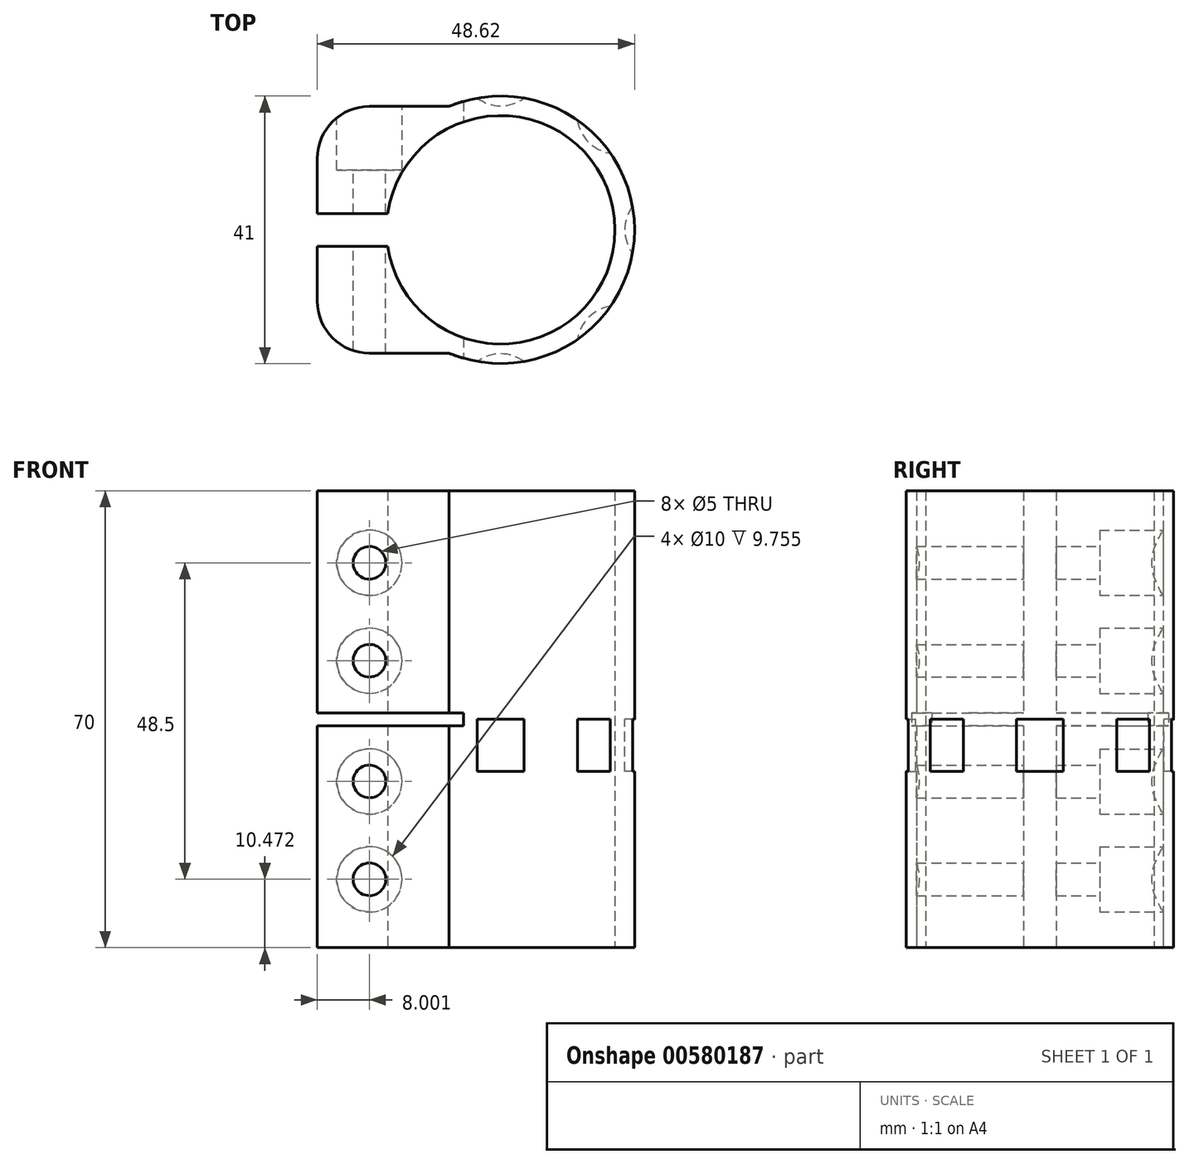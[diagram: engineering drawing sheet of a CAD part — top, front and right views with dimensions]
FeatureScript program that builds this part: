
annotation { "Feature Type Name" : "Feature", "Feature Type Description" : "" }
export const myFeature = defineFeature(function(context is Context, id is Id, definition is map)
    precondition{}
    {
        {
            var Q0;
            Q0=qCreatedBy(makeId("Top.planeOp"),FACE);
            var sketch = newSketch(context, id + "F0", { "sketchPlane" : qUnion([Q0])});
            skArc(sketch, "E0", {"start": v(-17.32, -2.5) * mm, "mid": v(17.5, 0) * mm, "end": v(-17.32, 2.5) * mm});
            skArc(sketch, "E1", {"start": v(-7.92, -18.9) * mm, "mid": v(20.5, 0) * mm, "end": v(-7.92, 18.9) * mm});
            skLineSegment(sketch, "E2", {"start": v(-7.92, 18.9) * mm, "end": v(-20.12, 18.9) * mm});
            skLineSegment(sketch, "E3", {"start": v(-28.12, 10.9) * mm, "end": v(-28.12, 2.5) * mm});
            skLineSegment(sketch, "E4", {"start": v(-28.12, 2.5) * mm, "end": v(-17.32, 2.5) * mm});
            skPoint(sketch, "E5.visualSharp", {"position": v(-28.12, 18.9) * mm});
            skArc(sketch, "E5.filletArc", {"start": v(-20.12, 18.9) * mm, "mid": v(-25.78, 16.57) * mm, "end": v(-28.12, 10.9) * mm});
            skLineSegment(sketch, "E6", {"start": v(0, 0) * mm, "end": v(46.32, 0) * mm, "construction": true});
            skPoint(sketch, "E7.newPointA", {"position": v(-28.12, 10.9) * mm});
            skPoint(sketch, "E7.newPointB", {"position": v(-20.12, 18.9) * mm});
            skLineSegment(sketch, "E8.MirrorCS", {"start": v(-28.12, -2.5) * mm, "end": v(-17.32, -2.5) * mm});
            skLineSegment(sketch, "E9.MirrorCS", {"start": v(-28.12, -10.9) * mm, "end": v(-28.12, -2.5) * mm});
            skArc(sketch, "E10.MirrorCS", {"start": v(-20.12, -18.9) * mm, "mid": v(-25.78, -16.57) * mm, "end": v(-28.12, -10.9) * mm});
            skLineSegment(sketch, "E11.MirrorCS", {"start": v(-7.92, -18.9) * mm, "end": v(-20.12, -18.9) * mm});
            skSolve(sketch);
        }
        {
            var Q0;
            Q0 = qSketchRegion(id + "F0", true);
            extrude(context, id + "F1", {"entities" : qUnion([Q0]), "endBound" : BoundingType.SYMMETRIC, "depth" : 70 * mm, "offsetDistance" : 25 * mm});
        }
        {
            var Q0;
            Q0=makeQuery(id+"F1.opExtrude","SWEPT_FACE",FACE,{"disambiguationData":[OSD([sQuery(id+"F0.wireOp",EDGE,"E2")])]});
            var sketch = newSketch(context, id + "F2", { "sketchPlane" : qUnion([Q0])});
            skPoint(sketch, "E12", {"position": v(20.12, 23.97) * mm});
            skPoint(sketch, "E13", {"position": v(20.12, 8.97) * mm});
            skPoint(sketch, "E14", {"position": v(20.12, -9.53) * mm});
            skPoint(sketch, "E15", {"position": v(20.12, -24.53) * mm});
            skPoint(sketch, "E16", {"position": v(0, -0.28) * mm});
            skSolve(sketch);
        }
        {
            var Q0;
            Q0=sQuery(id+"F2.wireOp",VERTEX,"E12");
            var Q1;
            Q1=sQuery(id+"F2.wireOp",VERTEX,"E13");
            var Q2;
            Q2=sQuery(id+"F2.wireOp",VERTEX,"E14");
            var Q3;
            Q3=sQuery(id+"F2.wireOp",VERTEX,"E15");
            var Q4;
            Q4=makeQuery(id+"F1.opExtrude","SWEPT_BODY",BODY,{"disambiguationData":[OSD([sQuery(id+"F0.wireOp",EDGE,"E0"),sQuery(id+"F0.wireOp",EDGE,"E1"),sQuery(id+"F0.wireOp",EDGE,"E2"),sQuery(id+"F0.wireOp",EDGE,"E3"),sQuery(id+"F0.wireOp",EDGE,"E4"),sQuery(id+"F0.wireOp",EDGE,"E5.filletArc"),sQuery(id+"F0.wireOp",EDGE,"E8.MirrorCS"),sQuery(id+"F0.wireOp",EDGE,"E9.MirrorCS"),sQuery(id+"F0.wireOp",EDGE,"E10.MirrorCS"),sQuery(id+"F0.wireOp",EDGE,"E11.MirrorCS")])]});
            hole(context, id + "F3", {"style" : HoleStyle.C_BORE, "endStyle" : HoleEndStyle.THROUGH, "holeDiameter" : 5 * mm, "cBoreDiameter" : 10 * mm, "cBoreDepth" : 8 * mm, "majorDiameter" : 5 * mm, "isTappedThrough" : true, "tappedDepth" : 12 * mm, "tapClearance" : 3, "locations" : qUnion([Q0, Q1, Q2, Q3]), "scope" : qUnion([Q4])});
        }
        {
            var Q0;
            Q0=qCreatedBy(makeId("Front.planeOp"),FACE);
            var sketch = newSketch(context, id + "F4", { "sketchPlane" : qUnion([Q0])});
            skLineSegment(sketch, "E17.bottom", {"start": v(-28.12, 1) * mm, "end": v(-5.72, 1) * mm});
            skLineSegment(sketch, "E17.top", {"start": v(-28.12, -1) * mm, "end": v(-5.72, -1) * mm});
            skLineSegment(sketch, "E17.left", {"start": v(-28.12, 1) * mm, "end": v(-28.12, -1) * mm});
            skLineSegment(sketch, "E17.right", {"start": v(-5.72, 1) * mm, "end": v(-5.72, -1) * mm});
            skSolve(sketch);
        }
        {
            var Q0;
            Q0 = qSketchRegion(id + "F4", true);
            extrude(context, id + "F5", {"entities" : qUnion([Q0]), "operationType" : NewBodyOperationType.REMOVE, "endBound" : BoundingType.SYMMETRIC, "oppositeDirection" : true, "depth" : 50 * mm, "offsetDistance" : 25 * mm});
        }
        {
            var Q0;
            Q0=qCreatedBy(makeId("Top.planeOp"),FACE);
            var sketch = newSketch(context, id + "F6", { "sketchPlane" : qUnion([Q0])});
            skCircle(sketch, "E18", {"center": v(0, -25) * mm, "radius": 6 * mm});
            skCircle(sketch, "E19.1.0", {"center": v(17.68, -17.68) * mm, "radius": 6 * mm});
            skCircle(sketch, "E19.2.0", {"center": v(25, 0) * mm, "radius": 6 * mm});
            skCircle(sketch, "E19.3.0", {"center": v(17.68, 17.68) * mm, "radius": 6 * mm});
            skCircle(sketch, "E19.4.0", {"center": v(0, 25) * mm, "radius": 6 * mm});
            skPoint(sketch, "E19.center", {"position": v(0, 0) * mm});
            skLineSegment(sketch, "E19.anchor1", {"start": v(0, 0) * mm, "end": v(0, -25) * mm, "construction": true});
            skLineSegment(sketch, "E19.anchor2", {"start": v(0, 0) * mm, "end": v(0, 25) * mm, "construction": true});
            skSolve(sketch);
        }
        {
            var Q0;
            Q0 = qSketchRegion(id + "F6", true);
            extrude(context, id + "F7", {"entities" : qUnion([Q0]), "operationType" : NewBodyOperationType.REMOVE, "oppositeDirection" : true, "depth" : 8 * mm, "offsetDistance" : 25 * mm});
        }
    });
